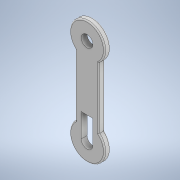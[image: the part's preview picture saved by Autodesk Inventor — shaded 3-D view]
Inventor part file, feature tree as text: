
AUTODESK INVENTOR PART (.ipt)
format: ipt  version: 2022 (Build 260153000, 153)  size: 158,208 bytes
history: native  units: in
note: dims shown in document units (in); Inventor stores cm internally (conversion verified against a paired STEP export)
features: extrude x2, sketch x2, fillet x1
ambient origin geometry x8: Origin, YZ Plane, XZ Plane, XY Plane, X Axis, Y Axis, Z Axis, Center Point
bodies: Solid1 (feature_tree)
feature tree (5):
  extrude  "Extrusion1"  Depth=0.7874in
  fillet  "Fillet1"  Radius=2.3622in
  extrude  "Extrusion2"  Depth=0.7874in
  sketch  "Sketch1"  dims[d0=0.7874in d1=1.6142in d2=2.3622in]
  sketch  "Sketch2"  dims[d3=0.7874in d4=5.9055in d5=0.7874in d6=5.9055in d7=2.3622in d8=0.7874in d9=0.3937in d10=0.0in d11=0.0787in d12=0.7874in d13=1.5945in d14=0.4188in d15=0.0in]
